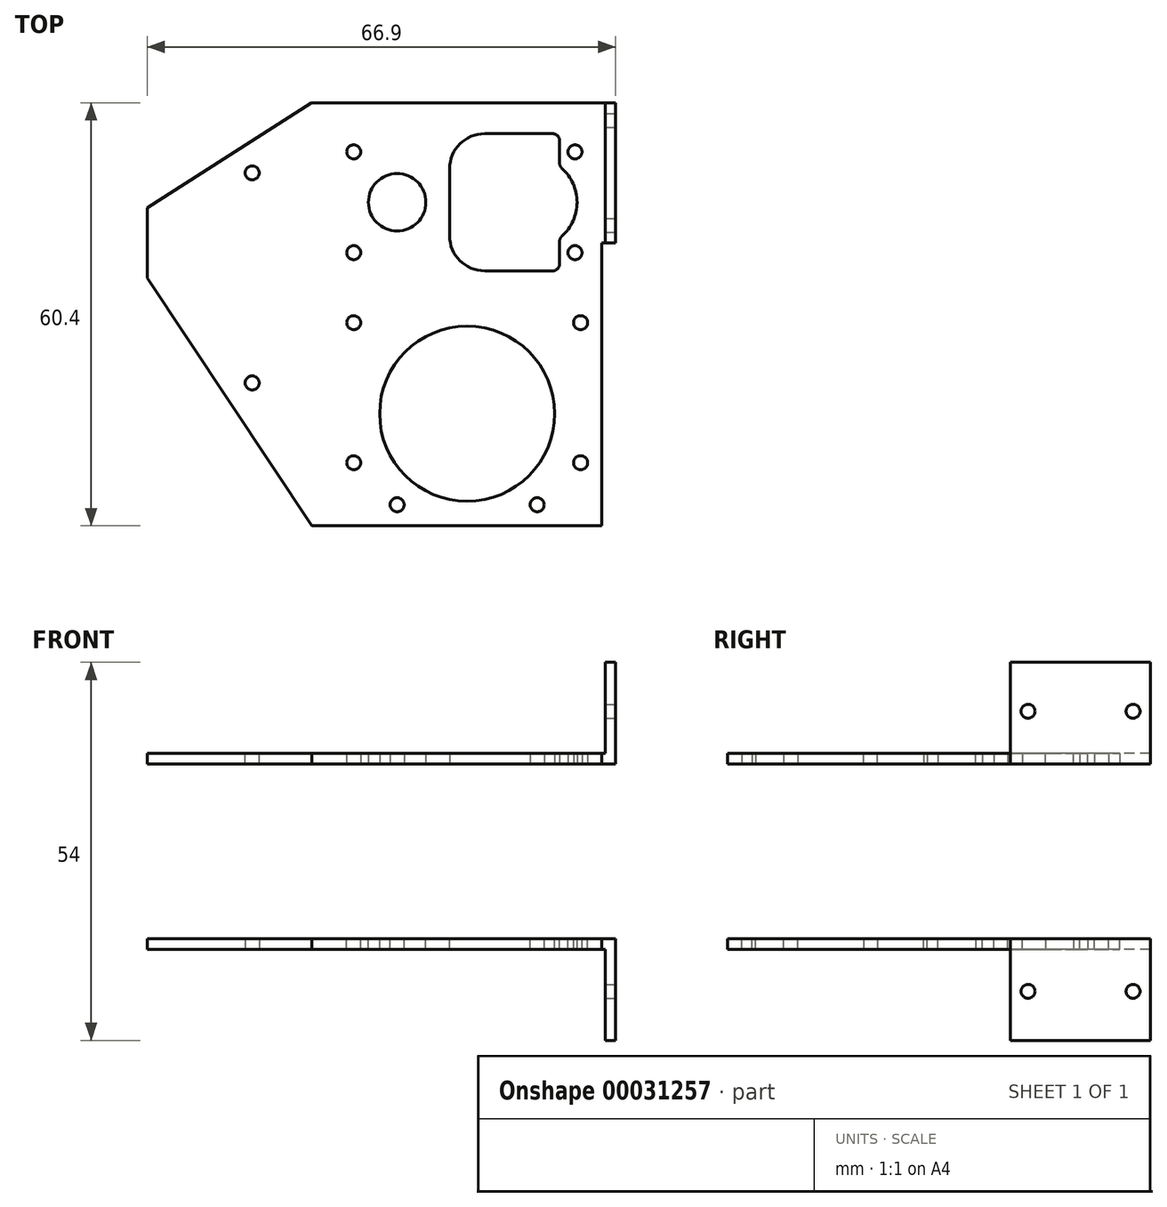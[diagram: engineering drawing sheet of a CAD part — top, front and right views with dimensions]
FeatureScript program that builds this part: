
annotation { "Feature Type Name" : "Feature", "Feature Type Description" : "" }
export const myFeature = defineFeature(function(context is Context, id is Id, definition is map)
    precondition{}
    {
        {
            var Q0;
            Q0=qCreatedBy(makeId("Top.planeOp"),FACE);
            var sketch = newSketch(context, id + "F0", { "sketchPlane" : qUnion([Q0])});
            skLineSegment(sketch, "E0.top", {"start": v(19.2, 14.2) * mm, "end": v(-19.2, 14.2) * mm});
            skLineSegment(sketch, "E0.left", {"start": v(19.2, -14.2) * mm, "end": v(19.2, 14.2) * mm});
            skLineSegment(sketch, "E0.right", {"start": v(-19.2, -14.2) * mm, "end": v(-19.2, 14.2) * mm});
            skPoint(sketch, "E0.middle", {"position": v(0, 0) * mm});
            skCircle(sketch, "E1", {"center": v(-10, 0) * mm, "radius": 4.1 * mm});
            skCircle(sketch, "E2", {"center": v(-16.2, 7.2) * mm, "radius": 1 * mm});
            skCircle(sketch, "E3", {"center": v(15.4, 7.2) * mm, "radius": 1 * mm});
            skLineSegment(sketch, "E4.bottom", {"start": v(2.5, 9.8) * mm, "end": v(12.2, 9.8) * mm});
            skLineSegment(sketch, "E4.top", {"start": v(2.5, -9.8) * mm, "end": v(12.2, -9.8) * mm});
            skLineSegment(sketch, "E4.left", {"start": v(-2.5, 4.8) * mm, "end": v(-2.5, -4.8) * mm});
            skLineSegment(sketch, "E4.right", {"start": v(13.2, 8.8) * mm, "end": v(13.2, 5.6) * mm});
            skPoint(sketch, "E4.middle", {"position": v(5.35, 0) * mm});
            skPoint(sketch, "E5.visualSharp", {"position": v(-2.5, 9.8) * mm});
            skArc(sketch, "E5.filletArc", {"start": v(2.5, 9.8) * mm, "mid": v(-1.04, 8.34) * mm, "end": v(-2.5, 4.8) * mm});
            skPoint(sketch, "E6.visualSharp", {"position": v(-2.5, -9.8) * mm});
            skArc(sketch, "E6.filletArc", {"start": v(-2.5, -4.8) * mm, "mid": v(-1.04, -8.34) * mm, "end": v(2.5, -9.8) * mm});
            skPoint(sketch, "E7.visualSharp", {"position": v(13.2, 9.8) * mm});
            skArc(sketch, "E7.filletArc", {"start": v(13.2, 8.8) * mm, "mid": v(12.9, 9.5) * mm, "end": v(12.2, 9.8) * mm});
            skPoint(sketch, "E8.visualSharp", {"position": v(13.2, -9.8) * mm});
            skArc(sketch, "E8.filletArc", {"start": v(12.2, -9.8) * mm, "mid": v(12.9, -9.5) * mm, "end": v(13.2, -8.8) * mm});
            skCircle(sketch, "E9.MirrorC", {"center": v(-16.2, -7.2) * mm, "radius": 1 * mm});
            skCircle(sketch, "E10.MirrorC", {"center": v(15.4, -7.2) * mm, "radius": 1 * mm});
            skArc(sketch, "E11", {"start": v(13.53, -4.84) * mm, "mid": v(15.7, 0) * mm, "end": v(13.53, 4.84) * mm});
            skLineSegment(sketch, "E12.trimOffspring", {"start": v(13.2, -5.6) * mm, "end": v(13.2, -8.8) * mm});
            skPoint(sketch, "E13.visualSharp", {"position": v(13.2, 5.12) * mm});
            skArc(sketch, "E13.filletArc", {"start": v(13.2, 5.6) * mm, "mid": v(13.29, 5.18) * mm, "end": v(13.53, 4.84) * mm});
            skPoint(sketch, "E14.visualSharp", {"position": v(13.2, -5.12) * mm});
            skArc(sketch, "E14.filletArc", {"start": v(13.53, -4.84) * mm, "mid": v(13.29, -5.18) * mm, "end": v(13.2, -5.6) * mm});
            skLineSegment(sketch, "E15.bottom", {"start": v(-19.2, -14.2) * mm, "end": v(19.2, -14.2) * mm, "construction": true});
            skLineSegment(sketch, "E15.top", {"start": v(-19.2, -46.2) * mm, "end": v(19.2, -46.2) * mm});
            skLineSegment(sketch, "E15.left", {"start": v(-19.2, -14.2) * mm, "end": v(-19.2, -46.2) * mm});
            skLineSegment(sketch, "E15.right", {"start": v(19.2, -14.2) * mm, "end": v(19.2, -46.2) * mm});
            skCircle(sketch, "E16", {"center": v(-10, -43.2) * mm, "radius": 1 * mm});
            skCircle(sketch, "E17.MirrorC", {"center": v(10, -43.2) * mm, "radius": 1 * mm});
            skCircle(sketch, "E18", {"center": v(16.2, -37.2) * mm, "radius": 1 * mm});
            skCircle(sketch, "E19", {"center": v(16.2, -17.2) * mm, "radius": 1 * mm});
            skCircle(sketch, "E20.MirrorC", {"center": v(-16.2, -17.2) * mm, "radius": 1 * mm});
            skCircle(sketch, "E21.MirrorC", {"center": v(-16.2, -37.2) * mm, "radius": 1 * mm});
            skCircle(sketch, "E22", {"center": v(0, -30.2) * mm, "radius": 12.5 * mm});
            skSolve(sketch);
        }
        {
            var Q0;
            Q0=qSketchRegion(id+"F0",true);
            extrude(context, id + "F1", {"entities" : qUnion([Q0]), "depth" : 1.5 * mm});
        }
        {
            var Q0;
            Q0=makeQuery(id+"F1.opExtrude","SWEPT_FACE",FACE,{"disambiguationData":[OSD([sQuery(id+"F0.wireOp",EDGE,"E0.left"),sQuery(id+"F0.wireOp",EDGE,"E15.right")])]});
            var sketch = newSketch(context, id + "F2", { "sketchPlane" : qUnion([Q0])});
            skLineSegment(sketch, "E23.bottom", {"start": v(14.2, 0) * mm, "end": v(-5.8, 0) * mm});
            skLineSegment(sketch, "E23.top", {"start": v(14.2, 1.5) * mm, "end": v(-5.8, 1.5) * mm});
            skLineSegment(sketch, "E23.left", {"start": v(14.2, 0) * mm, "end": v(14.2, 1.5) * mm});
            skLineSegment(sketch, "E23.right", {"start": v(-5.8, 0) * mm, "end": v(-5.8, 1.5) * mm});
            skSolve(sketch);
        }
        {
            var Q0;
            Q0=qSketchRegion(id+"F2",true);
            extrude(context, id + "F3", {"entities" : qUnion([Q0]), "operationType" : NewBodyOperationType.ADD, "depth" : 2 * mm});
        }
        {
            var Q0;
            Q0=makeQuery(id+"F3.boolean.opBoolean","MERGE",FACE,{"derivedFrom":[makeQuery(id+"F1.opExtrude","CAP_FACE",FACE,{"disambiguationData":[OSD([sQuery(id+"F0.wireOp",EDGE,"E0.top"),sQuery(id+"F0.wireOp",EDGE,"E0.left"),sQuery(id+"F0.wireOp",EDGE,"E0.right"),sQuery(id+"F0.wireOp",EDGE,"E1"),sQuery(id+"F0.wireOp",EDGE,"E2"),sQuery(id+"F0.wireOp",EDGE,"E3"),sQuery(id+"F0.wireOp",EDGE,"E4.bottom"),sQuery(id+"F0.wireOp",EDGE,"E4.top"),sQuery(id+"F0.wireOp",EDGE,"E4.left"),sQuery(id+"F0.wireOp",EDGE,"E4.right"),sQuery(id+"F0.wireOp",EDGE,"E5.filletArc"),sQuery(id+"F0.wireOp",EDGE,"E6.filletArc"),sQuery(id+"F0.wireOp",EDGE,"E7.filletArc"),sQuery(id+"F0.wireOp",EDGE,"E8.filletArc"),sQuery(id+"F0.wireOp",EDGE,"E9.MirrorC"),sQuery(id+"F0.wireOp",EDGE,"E10.MirrorC"),sQuery(id+"F0.wireOp",EDGE,"E11"),sQuery(id+"F0.wireOp",EDGE,"E12.trimOffspring"),sQuery(id+"F0.wireOp",EDGE,"E13.filletArc"),sQuery(id+"F0.wireOp",EDGE,"E14.filletArc"),sQuery(id+"F0.wireOp",EDGE,"E15.top"),sQuery(id+"F0.wireOp",EDGE,"E15.left"),sQuery(id+"F0.wireOp",EDGE,"E15.right"),sQuery(id+"F0.wireOp",EDGE,"E16"),sQuery(id+"F0.wireOp",EDGE,"E17.MirrorC"),sQuery(id+"F0.wireOp",EDGE,"E18"),sQuery(id+"F0.wireOp",EDGE,"E19"),sQuery(id+"F0.wireOp",EDGE,"E20.MirrorC"),sQuery(id+"F0.wireOp",EDGE,"E21.MirrorC")])],"isStart":false}),makeQuery(id+"F3.opExtrude","SWEPT_FACE",FACE,{"disambiguationData":[OSD([sQuery(id+"F2.wireOp",EDGE,"E23.top")])]})]});
            var sketch = newSketch(context, id + "F4", { "sketchPlane" : qUnion([Q0])});
            skLineSegment(sketch, "E24.bottom", {"start": v(19.7, 14.2) * mm, "end": v(21.2, 14.2) * mm});
            skLineSegment(sketch, "E24.top", {"start": v(19.7, -5.8) * mm, "end": v(21.2, -5.8) * mm});
            skLineSegment(sketch, "E24.left", {"start": v(19.7, 14.2) * mm, "end": v(19.7, -5.8) * mm});
            skLineSegment(sketch, "E24.right", {"start": v(21.2, 14.2) * mm, "end": v(21.2, -5.8) * mm});
            skSolve(sketch);
        }
        {
            var Q0;
            Q0=qSketchRegion(id+"F4",true);
            extrude(context, id + "F5", {"entities" : qUnion([Q0]), "operationType" : NewBodyOperationType.ADD, "depth" : 13 * mm});
        }
        {
            var Q0;
            Q0=qCreatedBy(makeId("Top.planeOp"),FACE);
            cPlane(context, id + "F6", {"entities" : qUnion([Q0]), "cplaneType" : CPlaneType.OFFSET, "offset" : (25 / 2) * mm, "oppositeDirection" : true, "width" : 150 * mm, "height" : 150 * mm});
        }
        {
            var Q0;
            Q0=makeQuery(id+"F1.opExtrude","SWEPT_BODY",BODY,{"disambiguationData":[OSD([sQuery(id+"F0.wireOp",EDGE,"E0.top"),sQuery(id+"F0.wireOp",EDGE,"E0.left"),sQuery(id+"F0.wireOp",EDGE,"E0.right"),sQuery(id+"F0.wireOp",EDGE,"E1"),sQuery(id+"F0.wireOp",EDGE,"E2"),sQuery(id+"F0.wireOp",EDGE,"E3"),sQuery(id+"F0.wireOp",EDGE,"E4.bottom"),sQuery(id+"F0.wireOp",EDGE,"E4.top"),sQuery(id+"F0.wireOp",EDGE,"E4.left"),sQuery(id+"F0.wireOp",EDGE,"E4.right"),sQuery(id+"F0.wireOp",EDGE,"E5.filletArc"),sQuery(id+"F0.wireOp",EDGE,"E6.filletArc"),sQuery(id+"F0.wireOp",EDGE,"E7.filletArc"),sQuery(id+"F0.wireOp",EDGE,"E8.filletArc"),sQuery(id+"F0.wireOp",EDGE,"E9.MirrorC"),sQuery(id+"F0.wireOp",EDGE,"E10.MirrorC"),sQuery(id+"F0.wireOp",EDGE,"E11"),sQuery(id+"F0.wireOp",EDGE,"E12.trimOffspring"),sQuery(id+"F0.wireOp",EDGE,"E13.filletArc"),sQuery(id+"F0.wireOp",EDGE,"E14.filletArc"),sQuery(id+"F0.wireOp",EDGE,"E15.top"),sQuery(id+"F0.wireOp",EDGE,"E15.left"),sQuery(id+"F0.wireOp",EDGE,"E15.right"),sQuery(id+"F0.wireOp",EDGE,"E16"),sQuery(id+"F0.wireOp",EDGE,"E17.MirrorC"),sQuery(id+"F0.wireOp",EDGE,"E18"),sQuery(id+"F0.wireOp",EDGE,"E19"),sQuery(id+"F0.wireOp",EDGE,"E20.MirrorC"),sQuery(id+"F0.wireOp",EDGE,"E21.MirrorC")])]});
            var Q1;
            Q1=qCreatedBy(id+"F6.planeOp",FACE);
            mirror(context, id + "F7", {"entities" : qUnion([Q0]), "mirrorPlane" : qUnion([Q1])});
        }
        {
            var Q0;
            Q0=makeQuery(id+"F7.opPattern","COPY",FACE,{"derivedFrom":makeQuery(id+"F5.boolean.opBoolean","MERGE",FACE,{"derivedFrom":[makeQuery(id+"F3.opExtrude","CAP_FACE",FACE,{"disambiguationData":[OSD([sQuery(id+"F2.wireOp",EDGE,"E23.bottom"),sQuery(id+"F2.wireOp",EDGE,"E23.top"),sQuery(id+"F2.wireOp",EDGE,"E23.left"),sQuery(id+"F2.wireOp",EDGE,"E23.right")])],"isStart":false}),makeQuery(id+"F5.opExtrude","SWEPT_FACE",FACE,{"disambiguationData":[OSD([sQuery(id+"F4.wireOp",EDGE,"E24.right")])]})]}),"instanceName":"1"});
            var sketch = newSketch(context, id + "F8", { "sketchPlane" : qUnion([Q0])});
            skCircle(sketch, "E25", {"center": v(11.7, 7.5) * mm, "radius": 1 * mm});
            skCircle(sketch, "E26", {"center": v(-3.3, 7.5) * mm, "radius": 1 * mm});
            skCircle(sketch, "E27.MirrorC", {"center": v(11.7, -32.5) * mm, "radius": 1 * mm});
            skCircle(sketch, "E28.MirrorC", {"center": v(-3.3, -32.5) * mm, "radius": 1 * mm});
            skSolve(sketch);
        }
        {
            var Q0;
            Q0=qSketchRegion(id+"F8",true);
            extrude(context, id + "F9", {"entities" : qUnion([Q0]), "operationType" : NewBodyOperationType.REMOVE, "endBound" : BoundingType.UP_TO_NEXT, "oppositeDirection" : true, "depth" : 25 * mm});
        }
        {
            var Q0;
            Q0=makeQuery(id+"F1.opExtrude","SWEPT_FACE",FACE,{"disambiguationData":[OSD([sQuery(id+"F0.wireOp",EDGE,"E0.right"),sQuery(id+"F0.wireOp",EDGE,"E15.left")])]});
            var sketch = newSketch(context, id + "F10", { "sketchPlane" : qUnion([Q0])});
            skLineSegment(sketch, "E29.bottom", {"start": v(-14.2, 0) * mm, "end": v(46.2, 0) * mm});
            skLineSegment(sketch, "E29.top", {"start": v(-14.2, 1.5) * mm, "end": v(46.2, 1.5) * mm});
            skLineSegment(sketch, "E29.left", {"start": v(-14.2, 0) * mm, "end": v(-14.2, 1.5) * mm});
            skLineSegment(sketch, "E29.right", {"start": v(46.2, 0) * mm, "end": v(46.2, 1.5) * mm});
            skSolve(sketch);
        }
        {
            var Q0;
            Q0=qSketchRegion(id+"F10",true);
            extrude(context, id + "F11", {"entities" : qUnion([Q0]), "operationType" : NewBodyOperationType.ADD, "depth" : (25 + 1.5) * mm});
        }
        {
            var Q0;
            Q0=makeQuery(id+"F11.boolean.opBoolean","MERGE",FACE,{"derivedFrom":[makeQuery(id+"F3.boolean.opBoolean","MERGE",FACE,{"derivedFrom":[makeQuery(id+"F1.opExtrude","CAP_FACE",FACE,{"disambiguationData":[OSD([sQuery(id+"F0.wireOp",EDGE,"E0.top"),sQuery(id+"F0.wireOp",EDGE,"E0.left"),sQuery(id+"F0.wireOp",EDGE,"E0.right"),sQuery(id+"F0.wireOp",EDGE,"E1"),sQuery(id+"F0.wireOp",EDGE,"E2"),sQuery(id+"F0.wireOp",EDGE,"E3"),sQuery(id+"F0.wireOp",EDGE,"E4.bottom"),sQuery(id+"F0.wireOp",EDGE,"E4.top"),sQuery(id+"F0.wireOp",EDGE,"E4.left"),sQuery(id+"F0.wireOp",EDGE,"E4.right"),sQuery(id+"F0.wireOp",EDGE,"E5.filletArc"),sQuery(id+"F0.wireOp",EDGE,"E6.filletArc"),sQuery(id+"F0.wireOp",EDGE,"E7.filletArc"),sQuery(id+"F0.wireOp",EDGE,"E8.filletArc"),sQuery(id+"F0.wireOp",EDGE,"E9.MirrorC"),sQuery(id+"F0.wireOp",EDGE,"E10.MirrorC"),sQuery(id+"F0.wireOp",EDGE,"E11"),sQuery(id+"F0.wireOp",EDGE,"E12.trimOffspring"),sQuery(id+"F0.wireOp",EDGE,"E13.filletArc"),sQuery(id+"F0.wireOp",EDGE,"E14.filletArc"),sQuery(id+"F0.wireOp",EDGE,"E15.top"),sQuery(id+"F0.wireOp",EDGE,"E15.left"),sQuery(id+"F0.wireOp",EDGE,"E15.right"),sQuery(id+"F0.wireOp",EDGE,"E16"),sQuery(id+"F0.wireOp",EDGE,"E17.MirrorC"),sQuery(id+"F0.wireOp",EDGE,"E18"),sQuery(id+"F0.wireOp",EDGE,"E19"),sQuery(id+"F0.wireOp",EDGE,"E20.MirrorC"),sQuery(id+"F0.wireOp",EDGE,"E21.MirrorC")])],"isStart":false}),makeQuery(id+"F3.opExtrude","SWEPT_FACE",FACE,{"disambiguationData":[OSD([sQuery(id+"F2.wireOp",EDGE,"E23.top")])]})]}),makeQuery(id+"F11.opExtrude","SWEPT_FACE",FACE,{"disambiguationData":[OSD([sQuery(id+"F10.wireOp",EDGE,"E29.top")])]})]});
            var sketch = newSketch(context, id + "F12", { "sketchPlane" : qUnion([Q0])});
            skLineSegment(sketch, "E30", {"start": v(-20.7, 14.2) * mm, "end": v(-20.7, -46.2) * mm, "construction": true});
            skLineSegment(sketch, "E31", {"start": v(-22.25, 14.2) * mm, "end": v(-45.7, -0.8) * mm});
            skLineSegment(sketch, "E32", {"start": v(-45.7, -0.8) * mm, "end": v(-45.7, -10.8) * mm});
            skLineSegment(sketch, "E33", {"start": v(-45.7, -10.8) * mm, "end": v(-22.2, -46.2) * mm});
            skLineSegment(sketch, "E34", {"start": v(-22.2, -46.2) * mm, "end": v(-45.7, -46.2) * mm});
            skLineSegment(sketch, "E35", {"start": v(-45.7, -46.2) * mm, "end": v(-45.7, -10.8) * mm});
            skLineSegment(sketch, "E36", {"start": v(-22.25, 14.2) * mm, "end": v(-45.7, 14.2) * mm});
            skLineSegment(sketch, "E37", {"start": v(-45.7, 14.2) * mm, "end": v(-45.7, -0.8) * mm});
            skCircle(sketch, "E38", {"center": v(-30.7, 4.2) * mm, "radius": 1 * mm});
            skCircle(sketch, "E39", {"center": v(-30.7, -25.8) * mm, "radius": 1 * mm});
            skLineSegment(sketch, "E40", {"start": v(-30.7, 4.2) * mm, "end": v(-30.7, -25.8) * mm, "construction": true});
            skSolve(sketch);
        }
        {
            var Q0;
            Q0=qSketchRegion(id+"F12",true);
            extrude(context, id + "F13", {"entities" : qUnion([Q0]), "operationType" : NewBodyOperationType.REMOVE, "endBound" : BoundingType.UP_TO_NEXT, "oppositeDirection" : true, "depth" : 25 * mm});
        }
        {
            var Q0;
            Q0=makeQuery(id+"F1.opExtrude","SWEPT_BODY",BODY,{"disambiguationData":[OSD([sQuery(id+"F0.wireOp",EDGE,"E0.top"),sQuery(id+"F0.wireOp",EDGE,"E0.left"),sQuery(id+"F0.wireOp",EDGE,"E0.right"),sQuery(id+"F0.wireOp",EDGE,"E1"),sQuery(id+"F0.wireOp",EDGE,"E2"),sQuery(id+"F0.wireOp",EDGE,"E3"),sQuery(id+"F0.wireOp",EDGE,"E4.bottom"),sQuery(id+"F0.wireOp",EDGE,"E4.top"),sQuery(id+"F0.wireOp",EDGE,"E4.left"),sQuery(id+"F0.wireOp",EDGE,"E4.right"),sQuery(id+"F0.wireOp",EDGE,"E5.filletArc"),sQuery(id+"F0.wireOp",EDGE,"E6.filletArc"),sQuery(id+"F0.wireOp",EDGE,"E7.filletArc"),sQuery(id+"F0.wireOp",EDGE,"E8.filletArc"),sQuery(id+"F0.wireOp",EDGE,"E9.MirrorC"),sQuery(id+"F0.wireOp",EDGE,"E10.MirrorC"),sQuery(id+"F0.wireOp",EDGE,"E11"),sQuery(id+"F0.wireOp",EDGE,"E12.trimOffspring"),sQuery(id+"F0.wireOp",EDGE,"E13.filletArc"),sQuery(id+"F0.wireOp",EDGE,"E14.filletArc"),sQuery(id+"F0.wireOp",EDGE,"E15.top"),sQuery(id+"F0.wireOp",EDGE,"E15.left"),sQuery(id+"F0.wireOp",EDGE,"E15.right"),sQuery(id+"F0.wireOp",EDGE,"E16"),sQuery(id+"F0.wireOp",EDGE,"E17.MirrorC"),sQuery(id+"F0.wireOp",EDGE,"E18"),sQuery(id+"F0.wireOp",EDGE,"E19"),sQuery(id+"F0.wireOp",EDGE,"E20.MirrorC"),sQuery(id+"F0.wireOp",EDGE,"E21.MirrorC")])]});
            var Q1;
            Q1=qCreatedBy(id+"F6.planeOp",FACE);
            mirror(context, id + "F14", {"operationType" : NewBodyOperationType.ADD, "entities" : qUnion([Q0]), "mirrorPlane" : qUnion([Q1])});
        }
        {
            var Q0;
            Q0=qCreatedBy(makeId("Top.planeOp"),FACE);
            cPlane(context, id + "F15", {"entities" : qUnion([Q0]), "cplaneType" : CPlaneType.OFFSET, "offset" : 25 * mm, "width" : 150 * mm, "height" : 150 * mm});
        }
        {
            var Q0;
            Q0=qCreatedBy(id+"F15.planeOp",FACE);
            var sketch = newSketch(context, id + "F16", { "sketchPlane" : qUnion([Q0])});
            skLineSegment(sketch, "E41.0.0", {"start": v(19.7, 14.2) * mm, "end": v(-22.25, 14.2) * mm, "construction": true});
            skLineSegment(sketch, "E41.0.1", {"start": v(-22.25, 14.2) * mm, "end": v(-45.7, -0.8) * mm});
            skLineSegment(sketch, "E41.0.2", {"start": v(-45.7, -0.8) * mm, "end": v(-45.7, -10.8) * mm});
            skLineSegment(sketch, "E41.0.3", {"start": v(-45.7, -10.8) * mm, "end": v(-22.2, -46.2) * mm});
            skLineSegment(sketch, "E41.0.4", {"start": v(-22.2, -46.2) * mm, "end": v(19.2, -46.2) * mm, "construction": true});
            skLineSegment(sketch, "E41.0.5", {"start": v(19.2, -46.2) * mm, "end": v(19.2, -5.8) * mm, "construction": true});
            skLineSegment(sketch, "E41.0.6", {"start": v(19.2, -5.8) * mm, "end": v(19.7, -5.8) * mm, "construction": true});
            skLineSegment(sketch, "E41.0.7", {"start": v(19.7, -5.8) * mm, "end": v(19.7, 14.2) * mm, "construction": true});
            skLineSegment(sketch, "E42", {"start": v(-22.25, 14.2) * mm, "end": v(-22.2, -46.2) * mm});
            skCircle(sketch, "E43.0", {"center": v(-30.7, 4.2) * mm, "radius": 1 * mm});
            skCircle(sketch, "E43.1", {"center": v(-30.7, -25.8) * mm, "radius": 1 * mm});
            skCircle(sketch, "E43.2", {"center": v(-30.7, 4.2) * mm, "radius": 1 * mm});
            skCircle(sketch, "E43.3", {"center": v(-30.7, -25.8) * mm, "radius": 1 * mm});
            skCircle(sketch, "E43.4", {"center": v(-30.7, 4.2) * mm, "radius": 1 * mm});
            skCircle(sketch, "E43.5", {"center": v(-30.7, -25.8) * mm, "radius": 1 * mm});
            skCircle(sketch, "E43.6", {"center": v(-30.7, -25.8) * mm, "radius": 1 * mm});
            skCircle(sketch, "E43.7", {"center": v(-30.7, 4.2) * mm, "radius": 1 * mm});
            skSolve(sketch);
        }
        {
            var Q0;
            Q0=qSketchRegion(id+"F16",true);
            extrude(context, id + "F17", {"entities" : qUnion([Q0]), "depth" : 25 * mm});
        }
        {
            var Q0;
            Q0=makeQuery(id+"F17.opExtrude","SWEPT_BODY",BODY,{"disambiguationData":[OSD([sQuery(id+"F16.wireOp",EDGE,"E41.0.1"),sQuery(id+"F16.wireOp",EDGE,"E41.0.2"),sQuery(id+"F16.wireOp",EDGE,"E41.0.3"),sQuery(id+"F16.wireOp",EDGE,"E42"),sQuery(id+"F16.wireOp",EDGE,"E43.6"),sQuery(id+"F16.wireOp",EDGE,"E43.7")])]});
            deleteBodies(context, id + "F18", {"entities" : qUnion([Q0])});
        }
    });
